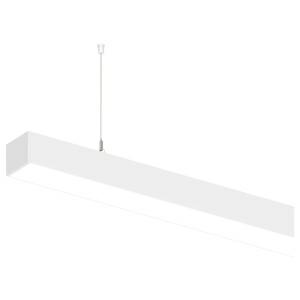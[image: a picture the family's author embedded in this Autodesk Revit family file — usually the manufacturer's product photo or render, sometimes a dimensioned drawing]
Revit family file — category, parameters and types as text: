
# Revit family: idaho_100_dir_ind_2000x102_hl_led_66w_7080lm_3000k_cri80_430-5210_9789
name_source: partatom
category: Lighting Fixtures
units: mm (PartAtom-declared; Revit-internal decimal feet)

## family parameters
Cut with Voids When Loaded = No
Host = Face
Light Source = No
Part Type = Normal
Room Calculation Point = No
Round Connector Dimension = Use Diameter
Shared = No

## types (1)
- 430-5210-D01 (13 x LED, 710 lm, 5.1 W, 3000K)
    Apparent Load = 66 VA
    CIE Flux Codes = 48 79 96 62 67
    Color Rendering = 1B/80…89
    Color Temperature = 3000K
    Default Elevation = 1800 mm
    Description = The pendant luminaire IDAHO 100 from the familiy IDAHO consists of aluminum. The ballast is integrated and allows for an operation with 220-240V (50/60Hz). IDAHO 100 (# 430-5210) ist not dimmable (on/off). The luminaire with direct and indirect illumination corresponds to protection class SK1 at IP20.
    Height = 90 mm
    Lamp = 13 x LED
    Lamp Light Flux = 710 lm
    Lamp Power = 5.1 W
    Lamp count = 13
    Length = 2000 mm  [stored 6.56168 ft]
    Luminous efficacy = 94 lm/W
    Manufacturer = Prolicht
    ModVariant = No
    Model = 430-5210
    Mounting Place = Ceiling
    Mounting Type = Pendant
    Number of Poles = 1
    OnlyDefault = Yes
    Power Factor = 1
    Product Name = IDAHO 100 DIR/IND 2000x102 HL LED 66W 7080lm 3000K CRI80
    Product group = Suspended profile lights
    ProductGroupID = 943
    Protection Class = Protection class
    Protection Degree = Degree of protection
    RLX_Detail_Level = 1
    RlxData = <blob elided: 66293 chars, md5=1cb6a5ca>
    Socket = socket
    Standby Power = 0 W
    System Light Flux = 6202 lm
    System Power = 66 W
    Type Image = 430-5210.jpg
    URL = http://relux.com
    VarID = 430-5210-d01
    Voltage = 0 V
    Weight = 0.00 kg
    Width = 102 mm

note: [stored X ft] marks values corroborated as IEEE doubles in the binary element streams (Revit-internal decimal feet)

## geometry (parser evidence)
native form markers: Blend x4, Sweep x14
no freeform markers — native parametric forms only
